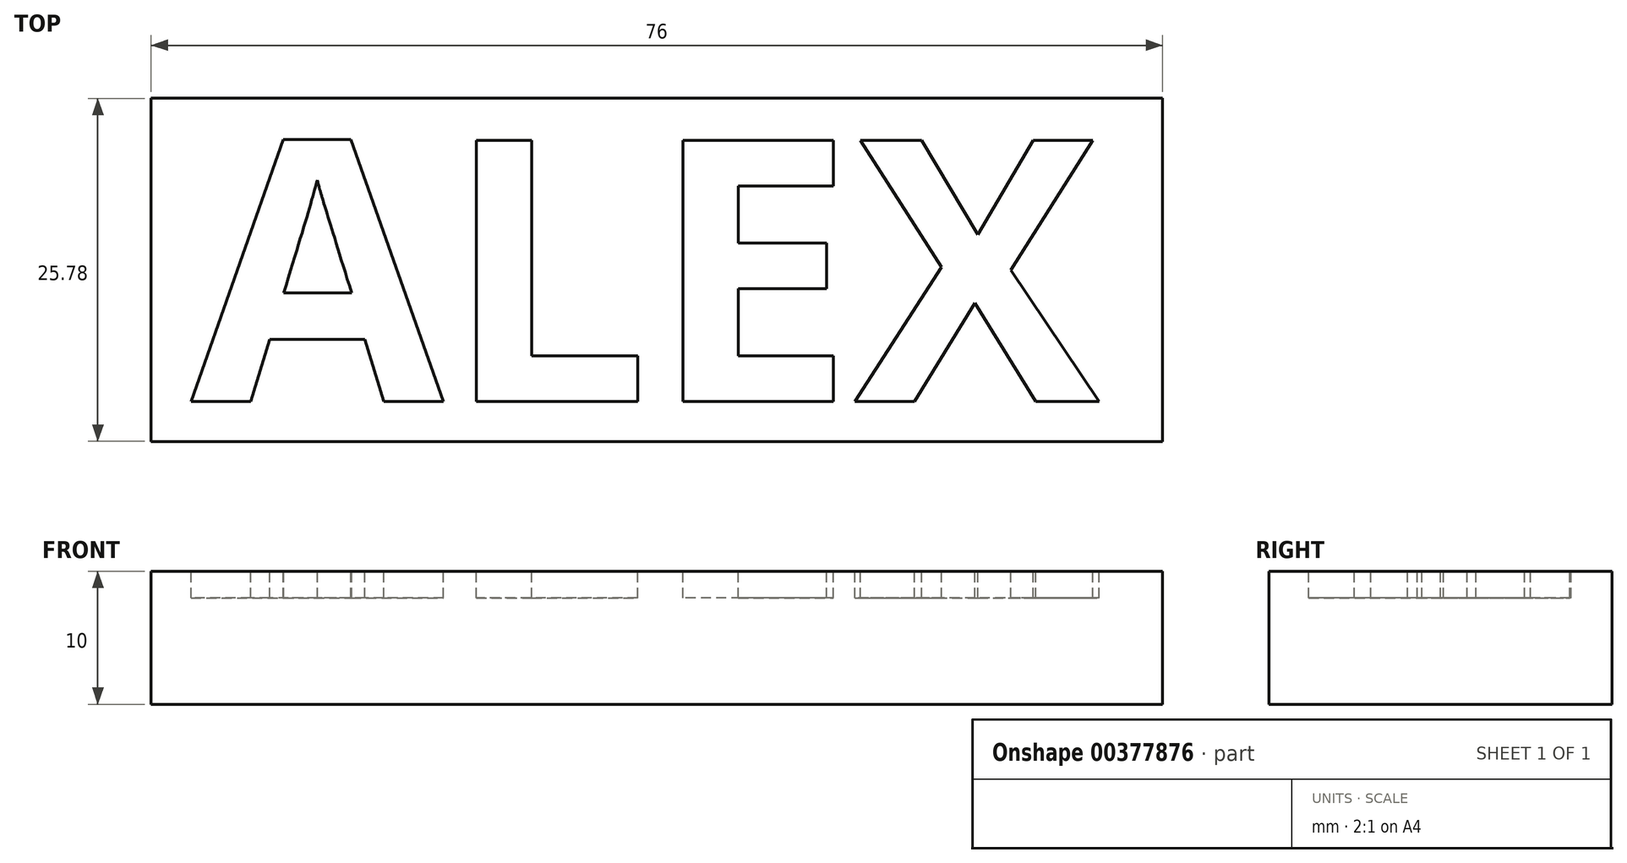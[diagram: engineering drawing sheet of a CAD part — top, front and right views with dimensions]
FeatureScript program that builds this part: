
annotation { "Feature Type Name" : "Feature", "Feature Type Description" : "" }
export const myFeature = defineFeature(function(context is Context, id is Id, definition is map)
    precondition{}
    {
        {
            var Q0;
            Q0=qCreatedBy(makeId("Top.planeOp"),FACE);
            var sketch = newSketch(context, id + "F0", { "sketchPlane" : qUnion([Q0])});
            skPoint(sketch, "E0.middle", {"position": v(0, 0) * mm});
            skText(sketch, "E1", { "text": "ALEX", "fontName": "OpenSans-Bold.ttf"});
            const initialGuessF0  = {"E1": [-0.035, -0.0099, 1, 0, 0.01979]};
            skSetInitialGuess(sketch, initialGuessF0);
            skSolve(sketch);
        }
        {
            var Q0;
            Q0=qCreatedBy(makeId("Top.planeOp"),FACE);
            var sketch = newSketch(context, id + "F1", { "sketchPlane" : qUnion([Q0])});
            skLineSegment(sketch, "E2.bottom", {"start": v(38, -12.9) * mm, "end": v(-38, -12.9) * mm});
            skLineSegment(sketch, "E2.top", {"start": v(38, 12.9) * mm, "end": v(-38, 12.9) * mm});
            skLineSegment(sketch, "E2.left", {"start": v(38, -12.9) * mm, "end": v(38, 12.9) * mm});
            skLineSegment(sketch, "E2.right", {"start": v(-38, -12.9) * mm, "end": v(-38, 12.9) * mm});
            skPoint(sketch, "E2.middle", {"position": v(0, 0) * mm});
            skSolve(sketch);
        }
        {
            var Q0;
            Q0 = qSketchRegion(id + "F1", true);
            extrude(context, id + "F2", {"entities" : qUnion([Q0]), "oppositeDirection" : true, "depth" : 10 * mm});
        }
        {
            var Q0;
            Q0 = qSketchRegion(id + "F0", true);
            extrude(context, id + "F3", {"entities" : qUnion([Q0]), "operationType" : NewBodyOperationType.REMOVE, "oppositeDirection" : true, "depth" : 2 * mm});
        }
    });
